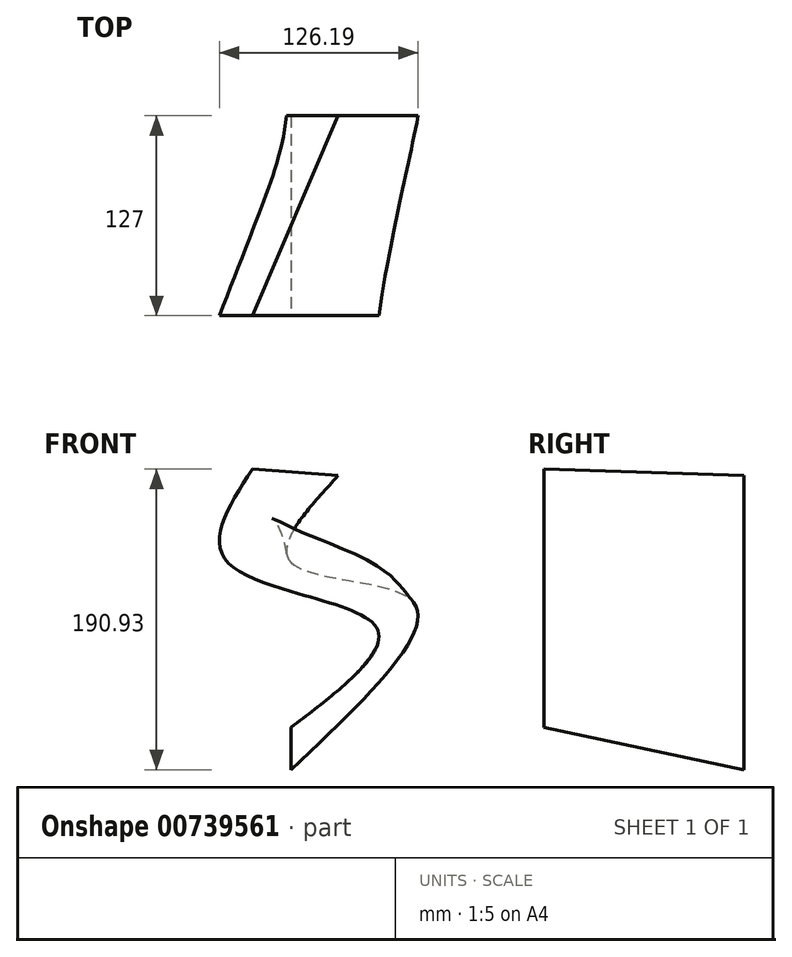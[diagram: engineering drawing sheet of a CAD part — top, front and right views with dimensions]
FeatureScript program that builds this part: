
annotation { "Feature Type Name" : "Feature", "Feature Type Description" : "" }
export const myFeature = defineFeature(function(context is Context, id is Id, definition is map)
    precondition{}
    {
        {
            var Q0;
            Q0=qCreatedBy(makeId("Front.planeOp"),FACE);
            var sketch = newSketch(context, id + "F0", { "sketchPlane" : qUnion([Q0])});
            skFitSpline(sketch, "E0", {"points": [v(29.87, 55.14) * mm, v(0, 0) * mm, v(77.24, -24.64) * mm, v(0, -131.65) * mm], "startDerivative": vector(-218.09, -237.85) * mm, "endDerivative": vector(-348.22, -329.77) * mm});
            skSolve(sketch);
        }
        {
            var Q0;
            Q0=qCreatedBy(makeId("Front.planeOp"),FACE);
            cPlane(context, id + "F1", {"entities" : qUnion([Q0]), "cplaneType" : CPlaneType.OFFSET, "offset" : 127 * mm, "width" : 152.4 * mm, "height" : 152.4 * mm});
        }
        {
            var Q0;
            Q0=qCreatedBy(id+"F1.planeOp",FACE);
            var sketch = newSketch(context, id + "F2", { "sketchPlane" : qUnion([Q0])});
            skFitSpline(sketch, "E1", {"points": [v(-24.6, 59.28) * mm, v(-40.13, 0) * mm, v(53.65, -40.53) * mm, v(0, -104.7) * mm], "startDerivative": vector(-150.95, -232.87) * mm, "endDerivative": vector(-286.12, -217.88) * mm});
            skSolve(sketch);
        }
        {
            var Q0;
            Q0=qCreatedBy(makeId("Right.planeOp"),FACE);
            var sketch = newSketch(context, id + "F3", { "sketchPlane" : qUnion([Q0])});
            skFitSpline(sketch, "E2", {"points": [v(-127, -18.38) * mm, v(-58.94, 22.3) * mm, v(0, 0) * mm], "startDerivative": vector(142.4, 100.2) * mm, "endDerivative": vector(153.64, -73.71) * mm});
            skSolve(sketch);
        }
        {
            var Q0;
            Q0=sQuery(id+"F0.wireOp",EDGE,"E0");
            var Q1;
            Q1=sQuery(id+"F2.wireOp",EDGE,"E1");
            var Q2;
            Q2=sQuery(id+"F3.wireOp",EDGE,"E2");
            loft(context, id + "F4", {"bodyType" : ToolBodyType.SURFACE, "addGuides" : true, "wireProfilesArray" : [{ "wireProfileEntities" : qUnion([Q0]) }, { "wireProfileEntities" : qUnion([Q1]) }], "guidesArray" : [{ "guideEntities" : qUnion([Q2]), "guideDerivativeType" : LoftGuideDerivativeType.DEFAULT, "guideDerivativeMagnitude" : 1 }]});
        }
    });
